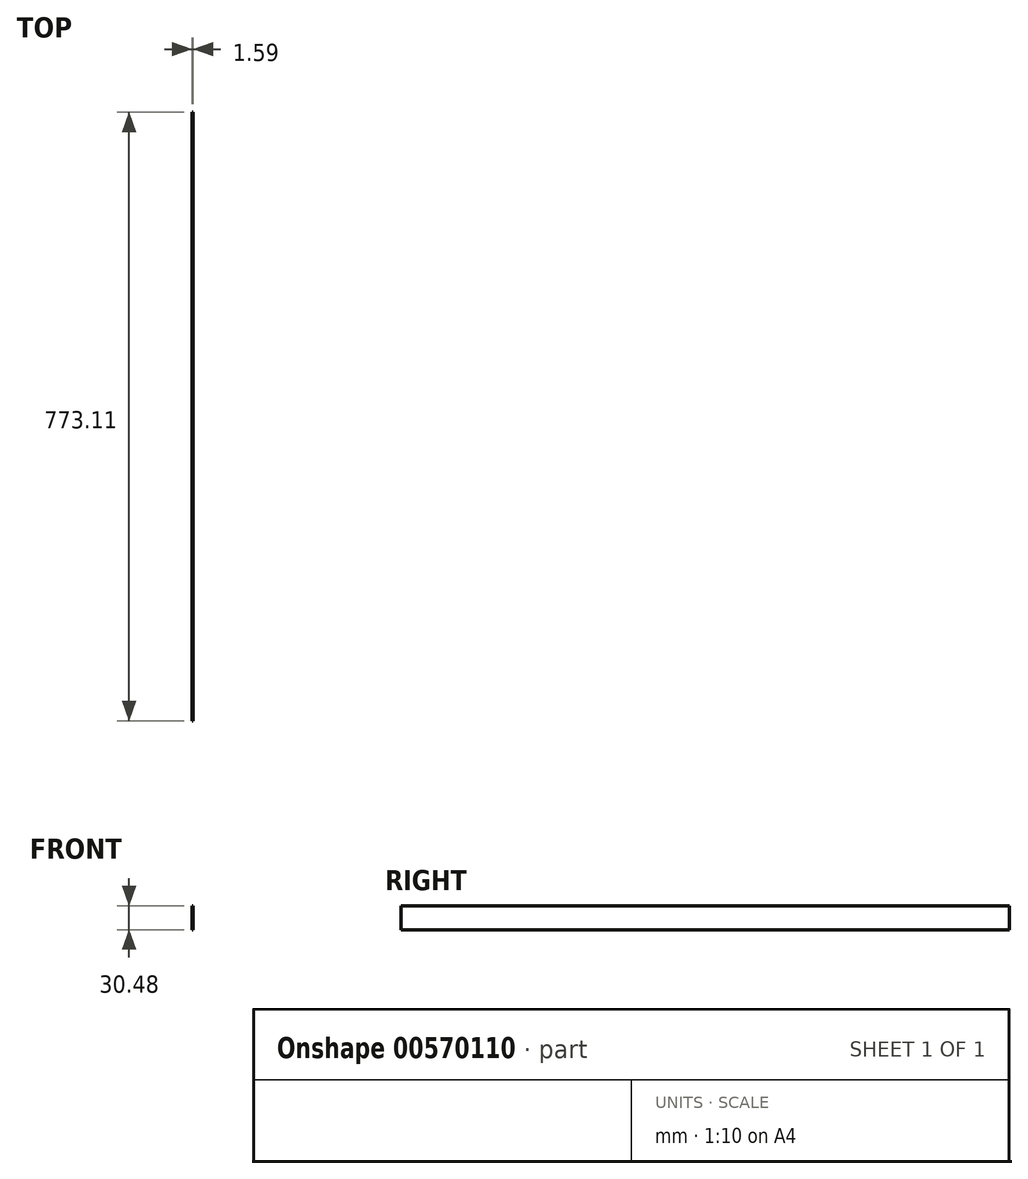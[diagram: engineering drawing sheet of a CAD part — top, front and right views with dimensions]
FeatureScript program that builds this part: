
annotation { "Feature Type Name" : "Feature", "Feature Type Description" : "" }
export const myFeature = defineFeature(function(context is Context, id is Id, definition is map)
    precondition{}
    {
        {
            var Q0;
            Q0=qCreatedBy(makeId("Front.planeOp"),FACE);
            var sketch = newSketch(context, id + "F0", { "sketchPlane" : qUnion([Q0])});
            skLineSegment(sketch, "E0.bottom", {"start": v(0, 0) * mm, "end": v(1.59, 0) * mm});
            skLineSegment(sketch, "E0.top", {"start": v(0, -30.48) * mm, "end": v(1.59, -30.48) * mm});
            skLineSegment(sketch, "E0.left", {"start": v(0, 0) * mm, "end": v(0, -30.48) * mm});
            skLineSegment(sketch, "E0.right", {"start": v(1.59, 0) * mm, "end": v(1.59, -30.48) * mm});
            skSolve(sketch);
        }
        {
            var Q0;
            Q0 = qSketchRegion(id + "F0", true);
            extrude(context, id + "F1", {"entities" : qUnion([Q0]), "depth" : 773.1 * mm, "offsetDistance" : 25.4 * mm});
        }
    });
